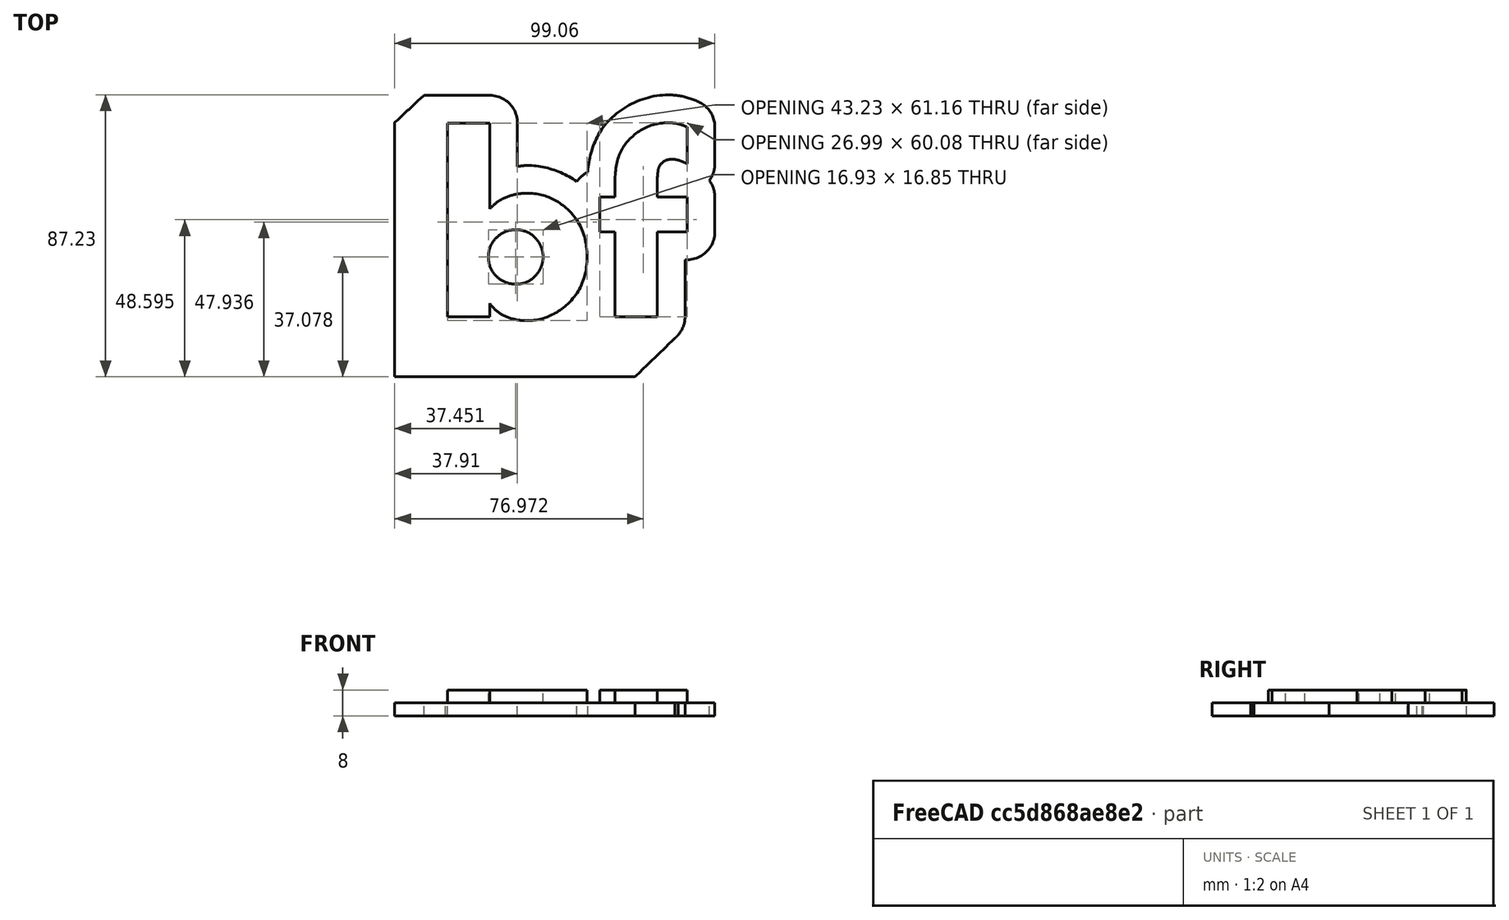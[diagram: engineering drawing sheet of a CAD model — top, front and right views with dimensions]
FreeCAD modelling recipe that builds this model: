
FCSTD DOCUMENT  (FreeCAD 0.16R6706 (Git))
Label: bf_logo
License: All rights reserved
LicenseURL: http://en.wikipedia.org/wiki/All_rights_reserved
objects: Part::Feature×5, Part::Extrusion×4, Part::Cut×1, Part::MultiFuse×1, Mesh::Feature×1
note: 11 computed .brp shape members not serialized (recipe doc carries the construction recipe); baked Part::Feature solids carry a one-line shape summary decoded from their .brp

FEATURE [Part::Feature] path4594
  shape: bbox 99.07 x 87.23 x 9.335e-06 mm, 0 faces, 0 solids (baked)
FEATURE [Part::Feature] path4146
  shape: bbox 43.23 x 61.16 x 5.739e-06 mm, 0 faces, 0 solids (baked)
FEATURE [Part::Feature] path4146001
  shape: bbox 16.93 x 16.85 x 5.739e-06 mm, 0 faces, 0 solids (baked)
FEATURE [Part::Feature] path4148
  shape: bbox 26.99 x 60.08 x 5.739e-06 mm, 0 faces, 0 solids (baked)
FEATURE [Part::Extrusion] Extrude  label="outline"
  Base = -> path4594
  Dir = (0,0,4)
  Solid = true
FEATURE [Part::Extrusion] Extrude001
  Base = -> path4146
  Dir = (0,0,8)
  Solid = true
FEATURE [Part::Extrusion] Extrude002  label="f"
  Base = -> path4148
  Dir = (0,0,8)
  Solid = true
FEATURE [Part::Extrusion] Extrude003
  Base = -> path4146001
  Dir = (0,0,8)
  Solid = true
FEATURE [Part::Cut] Cut  label="b"
  Base = -> Extrude001
  Tool = -> Extrude003
FEATURE [Part::MultiFuse] Fusion
  Shapes = -> [Extrude,Extrude002,Cut]
FEATURE [Part::Feature] Fusion001  label="bf_refined"
  shape: bbox 99.07 x 87.23 x 8 mm, 72 faces (baked)
FEATURE [Mesh::Feature] Mesh  label="bf_refined (Meshed)"
